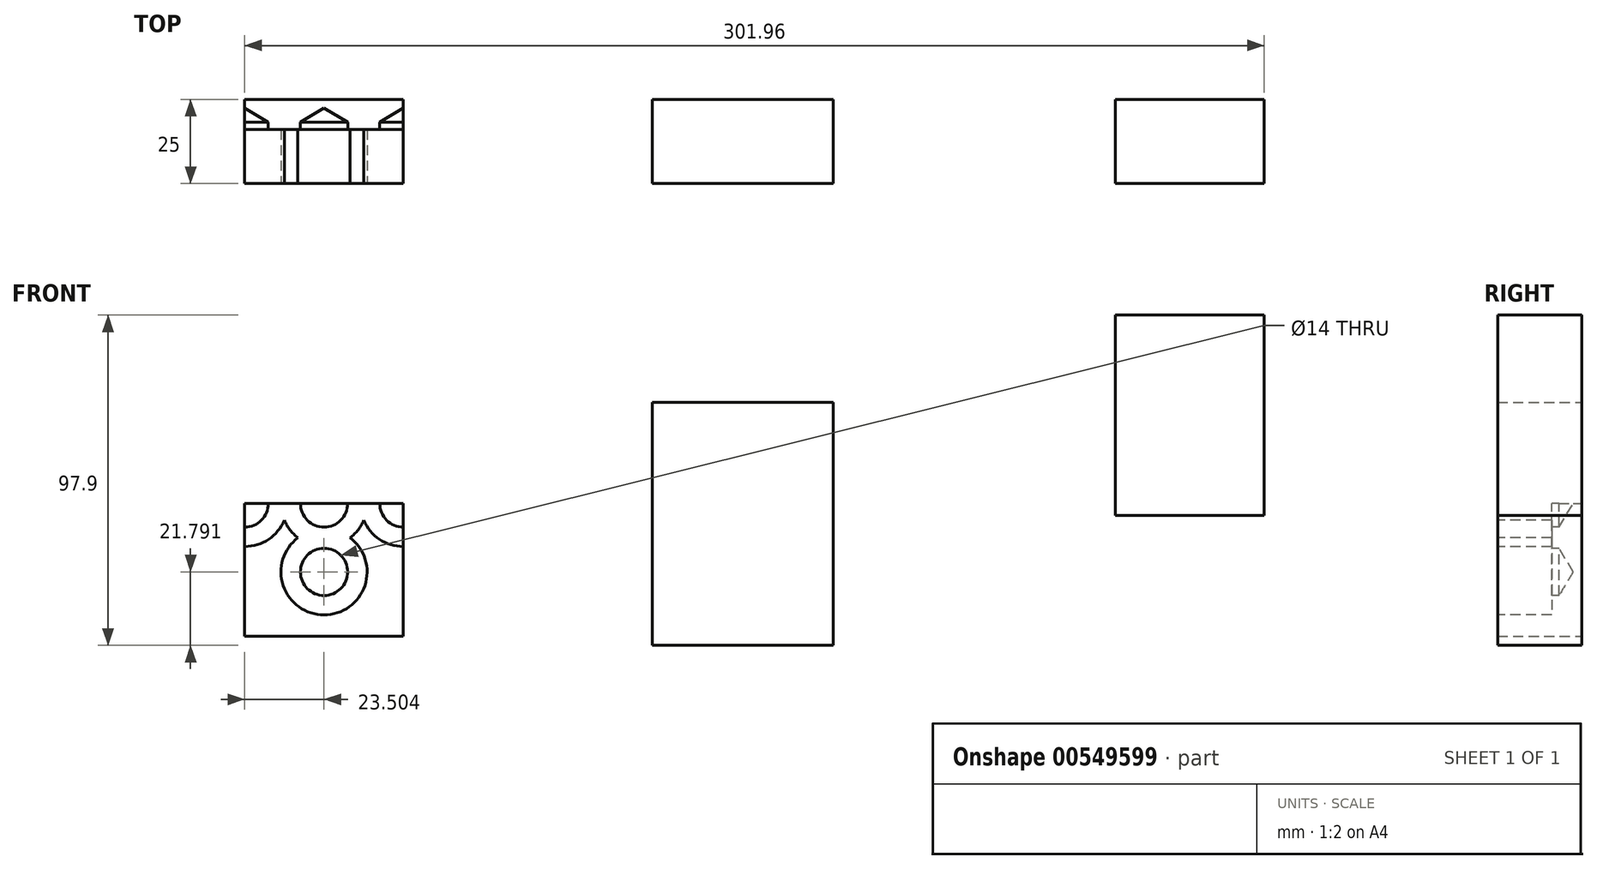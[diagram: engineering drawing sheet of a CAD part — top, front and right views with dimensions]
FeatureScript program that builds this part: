
annotation { "Feature Type Name" : "Feature", "Feature Type Description" : "" }
export const myFeature = defineFeature(function(context is Context, id is Id, definition is map)
    precondition{}
    {
        {
            var Q0;
            Q0=qCreatedBy(makeId("Front.planeOp"),FACE);
            var sketch = newSketch(context, id + "F0", { "sketchPlane" : qUnion([Q0])});
            skLineSegment(sketch, "E0.bottom", {"start": v(-167.79, -7.47) * mm, "end": v(-120.78, -7.47) * mm});
            skLineSegment(sketch, "E0.top", {"start": v(-167.79, -46.78) * mm, "end": v(-120.78, -46.78) * mm});
            skLineSegment(sketch, "E0.left", {"start": v(-167.79, -7.47) * mm, "end": v(-167.79, -46.78) * mm});
            skLineSegment(sketch, "E0.right", {"start": v(-120.78, -7.47) * mm, "end": v(-120.78, -46.78) * mm});
            skLineSegment(sketch, "E1.bottom", {"start": v(-47, 22.5) * mm, "end": v(6.53, 22.5) * mm});
            skLineSegment(sketch, "E1.top", {"start": v(-47, -49.53) * mm, "end": v(6.53, -49.53) * mm});
            skLineSegment(sketch, "E1.left", {"start": v(-47, 22.5) * mm, "end": v(-47, -49.53) * mm});
            skLineSegment(sketch, "E1.right", {"start": v(6.53, 22.5) * mm, "end": v(6.53, -49.53) * mm});
            skLineSegment(sketch, "E2.bottom", {"start": v(90.1, 48.37) * mm, "end": v(134.17, 48.37) * mm});
            skLineSegment(sketch, "E2.top", {"start": v(90.1, -11.05) * mm, "end": v(134.17, -11.05) * mm});
            skLineSegment(sketch, "E2.left", {"start": v(90.1, 48.37) * mm, "end": v(90.1, -11.05) * mm});
            skLineSegment(sketch, "E2.right", {"start": v(134.17, 48.37) * mm, "end": v(134.17, -11.05) * mm});
            skSolve(sketch);
        }
        {
            var Q0;
            Q0 = qSketchRegion(id + "F0", true);
            extrude(context, id + "F1", {"entities" : qUnion([Q0]), "depth" : 25 * mm, "offsetDistance" : 25 * mm});
        }
        {
            var Q0;
            Q0=makeQuery(id+"F1.opExtrude","CAP_FACE",FACE,{"disambiguationData":[OSD([sQuery(id+"F0.wireOp",EDGE,"E0.bottom"),sQuery(id+"F0.wireOp",EDGE,"E0.top"),sQuery(id+"F0.wireOp",EDGE,"E0.left"),sQuery(id+"F0.wireOp",EDGE,"E0.right")])],"isStart":false});
            var sketch = newSketch(context, id + "F2", { "sketchPlane" : qUnion([Q0])});
            skPoint(sketch, "E3", {"position": v(-167.79, -7.47) * mm});
            skPoint(sketch, "E4", {"position": v(-120.78, -7.47) * mm});
            skPoint(sketch, "E5", {"position": v(-144.29, -7.47) * mm});
            skPoint(sketch, "E6", {"position": v(-144.29, -27.74) * mm});
            skSolve(sketch);
        }
        {
            var Q0;
            Q0=sQuery(id+"F2.wireOp",VERTEX,"E3");
            var Q1;
            Q1=sQuery(id+"F2.wireOp",VERTEX,"E5");
            var Q2;
            Q2=sQuery(id+"F2.wireOp",VERTEX,"E4");
            var Q3;
            Q3=sQuery(id+"F2.wireOp",VERTEX,"E6");
            var Q4;
            Q4=makeQuery(id+"F1.opExtrude","SWEPT_BODY",BODY,{"disambiguationData":[OSD([sQuery(id+"F0.wireOp",EDGE,"E0.bottom"),sQuery(id+"F0.wireOp",EDGE,"E0.top"),sQuery(id+"F0.wireOp",EDGE,"E0.left"),sQuery(id+"F0.wireOp",EDGE,"E0.right")])]});
            hole(context, id + "F3", {"style" : HoleStyle.C_BORE, "endStyle" : HoleEndStyle.BLIND, "standardTappedOrClearance" : lookupTablePath({ "standard" : "ISO", "engagement" : "75%", "pitch" : "2 mm", "size" : "M16", "type" : "Tapped" }), "standardBlindInLast" : lookupTablePath({ "standard" : "ISO", "engagement" : "75%", "pitch" : "2 mm", "size" : "M16", "type" : "Tapped" }), "holeDiameter" : 14 * mm, "cBoreDiameter" : 25.5 * mm, "cBoreDepth" : 16 * mm, "showTappedDepth" : true, "holeDepth" : 18.2 * mm, "isTappedThrough" : true, "tappedDepth" : 12.2 * mm, "tapClearance" : 3, "startFromSketch" : true, "locations" : qUnion([Q0, Q1, Q2, Q3]), "scope" : qUnion([Q4]), "majorDiameter" : 16 * mm});
        }
    });
